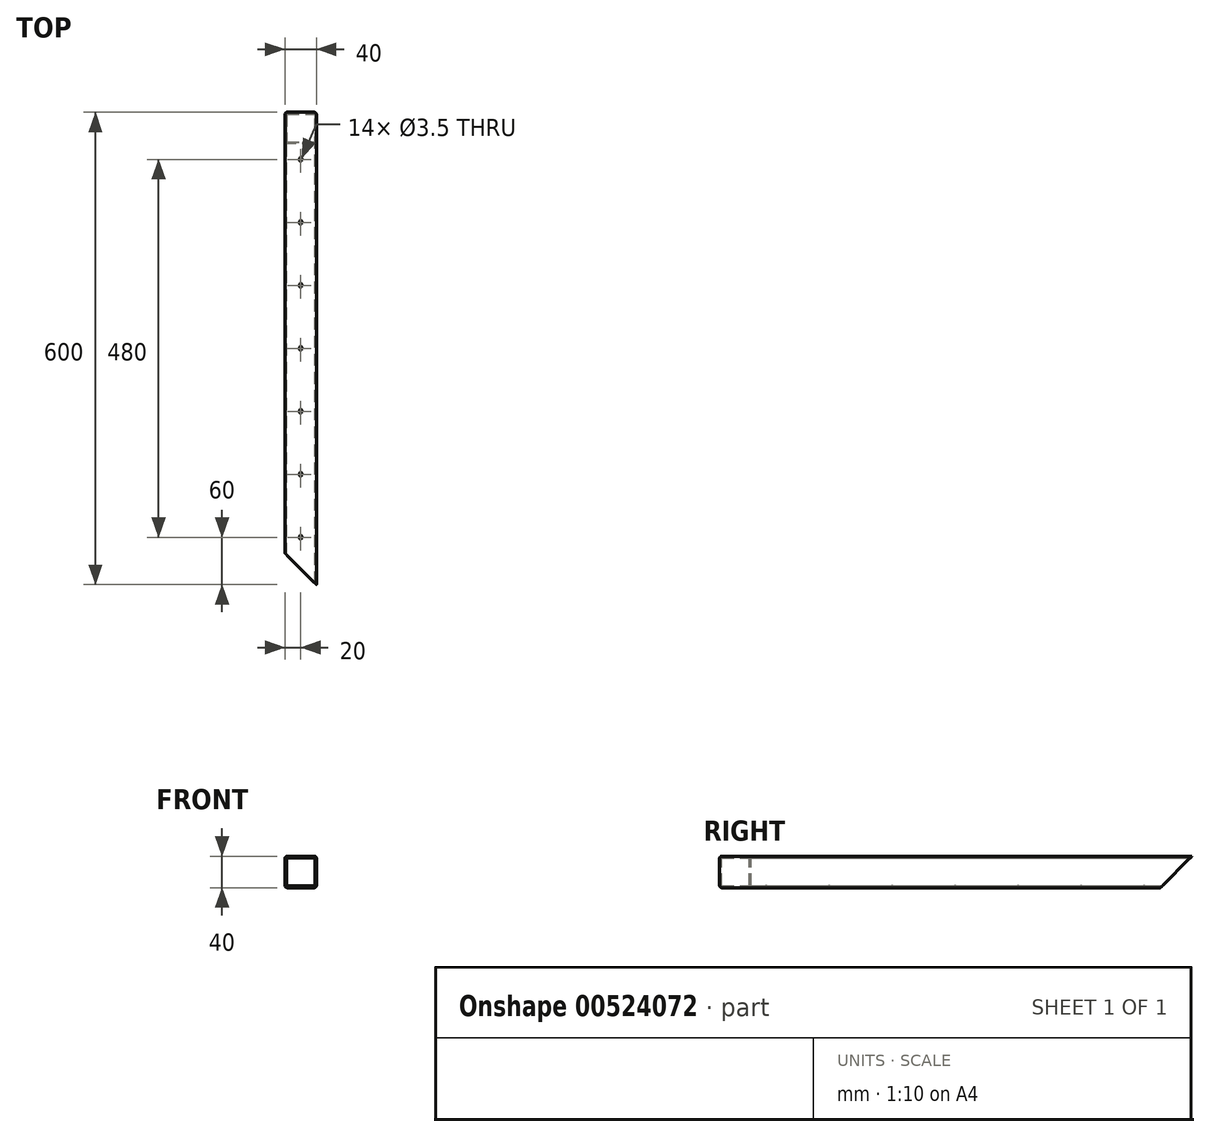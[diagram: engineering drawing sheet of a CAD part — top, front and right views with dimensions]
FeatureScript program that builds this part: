
annotation { "Feature Type Name" : "Feature", "Feature Type Description" : "" }
export const myFeature = defineFeature(function(context is Context, id is Id, definition is map)
    precondition{}
    {
        {
            assignVariable(context, id + "F0", {"name" : "R", "anyValue" : 3});
        }
        {
            assignVariable(context, id + "F1", {"name" : "W", "anyValue" : 2});
        }
        {
            var Q0;
            Q0=qCreatedBy(makeId("Front.planeOp"),FACE);
            var sketch = newSketch(context, id + "F2", { "sketchPlane" : qUnion([Q0])});
            skLineSegment(sketch, "E0.bottom", {"start": v(-20, 20) * mm, "end": v(20, 20) * mm});
            skLineSegment(sketch, "E0.top", {"start": v(-20, -20) * mm, "end": v(20, -20) * mm});
            skLineSegment(sketch, "E0.left", {"start": v(-20, 20) * mm, "end": v(-20, -20) * mm});
            skLineSegment(sketch, "E0.right", {"start": v(20, 20) * mm, "end": v(20, -20) * mm});
            skSolve(sketch);
        }
        {
            var Q0;
            Q0=qSketchRegion(id+"F2",true);
            extrude(context, id + "F3", {"entities" : qUnion([Q0]), "endBound" : BoundingType.SYMMETRIC, "depth" : 600 * mm, "offsetDistance" : 25 * mm});
        }
        {
            var Q0;
            Q0=makeQuery(id+"F3.opExtrude","SWEPT_EDGE",EDGE,{"disambiguationData":[OSD([sQuery(id+"F2.wireOp",EDGE,"E0.bottom"),sQuery(id+"F2.wireOp",EDGE,"E0.right")])]});
            var Q1;
            Q1=makeQuery(id+"F3.opExtrude","SWEPT_EDGE",EDGE,{"disambiguationData":[OSD([sQuery(id+"F2.wireOp",EDGE,"E0.bottom"),sQuery(id+"F2.wireOp",EDGE,"E0.left")])]});
            var Q2;
            Q2=makeQuery(id+"F3.opExtrude","SWEPT_EDGE",EDGE,{"disambiguationData":[OSD([sQuery(id+"F2.wireOp",EDGE,"E0.top"),sQuery(id+"F2.wireOp",EDGE,"E0.right")])]});
            var Q3;
            Q3=makeQuery(id+"F3.opExtrude","SWEPT_EDGE",EDGE,{"disambiguationData":[OSD([sQuery(id+"F2.wireOp",EDGE,"E0.top"),sQuery(id+"F2.wireOp",EDGE,"E0.left")])]});
            fillet(context, id + "F4", {"entities" : qUnion([Q0, Q1, Q2, Q3]), "radius" : (getVariable(context, 'R')) * mm, "tangentPropagation" : true, "allowEdgeOverflow" : false});
        }
        {
            var Q0;
            Q0=makeQuery(id+"F3.opExtrude","CAP_FACE",FACE,{"disambiguationData":[OSD([sQuery(id+"F2.wireOp",EDGE,"E0.bottom"),sQuery(id+"F2.wireOp",EDGE,"E0.top"),sQuery(id+"F2.wireOp",EDGE,"E0.left"),sQuery(id+"F2.wireOp",EDGE,"E0.right")])],"isStart":false});
            var Q1;
            Q1=makeQuery(id+"F3.opExtrude","CAP_FACE",FACE,{"disambiguationData":[OSD([sQuery(id+"F2.wireOp",EDGE,"E0.bottom"),sQuery(id+"F2.wireOp",EDGE,"E0.top"),sQuery(id+"F2.wireOp",EDGE,"E0.left"),sQuery(id+"F2.wireOp",EDGE,"E0.right")])],"isStart":true});
            shell(context, id + "F5", {"entities" : qUnion([Q0, Q1]), "thickness" : (getVariable(context, 'W')) * mm});
        }
        {
            var Q0;
            Q0=makeQuery(id+"F3.opExtrude","SWEPT_FACE",FACE,{"disambiguationData":[OSD([sQuery(id+"F2.wireOp",EDGE,"E0.left")])]});
            var sketch = newSketch(context, id + "F6", { "sketchPlane" : qUnion([Q0])});
            skLineSegment(sketch, "E1", {"start": v(-300, -20) * mm, "end": v(-260, -20) * mm});
            skLineSegment(sketch, "E2", {"start": v(-260, -20) * mm, "end": v(-300, 20) * mm});
            skLineSegment(sketch, "E3", {"start": v(-300, 20) * mm, "end": v(-300, -20) * mm});
            skSolve(sketch);
        }
        {
            var Q0;
            Q0=qSketchRegion(id+"F6",true);
            extrude(context, id + "F7", {"entities" : qUnion([Q0]), "operationType" : NewBodyOperationType.REMOVE, "endBound" : BoundingType.THROUGH_ALL, "oppositeDirection" : true, "depth" : 25 * mm, "offsetDistance" : 25 * mm});
        }
        {
            var Q0;
            Q0=makeQuery(id+"F3.opExtrude","SWEPT_FACE",FACE,{"disambiguationData":[OSD([sQuery(id+"F2.wireOp",EDGE,"E0.bottom")])]});
            var sketch = newSketch(context, id + "F8", { "sketchPlane" : qUnion([Q0])});
            skLineSegment(sketch, "E4.0", {"start": v(20, 297) * mm, "end": v(20, -300) * mm, "construction": true});
            skLineSegment(sketch, "E5", {"start": v(-20, -300) * mm, "end": v(20, -300) * mm});
            skLineSegment(sketch, "E6", {"start": v(20, -300) * mm, "end": v(-20, -260) * mm});
            skLineSegment(sketch, "E7", {"start": v(-20, -260) * mm, "end": v(-20, -300) * mm});
            skSolve(sketch);
        }
        {
            var Q0;
            Q0=qSketchRegion(id+"F8",true);
            extrude(context, id + "F9", {"entities" : qUnion([Q0]), "operationType" : NewBodyOperationType.REMOVE, "endBound" : BoundingType.THROUGH_ALL, "oppositeDirection" : true, "depth" : 25 * mm, "offsetDistance" : 25 * mm});
        }
        {
            var Q0;
            Q0=makeQuery(id+"F3.opExtrude","SWEPT_FACE",FACE,{"disambiguationData":[OSD([sQuery(id+"F2.wireOp",EDGE,"E0.top")])]});
            var sketch = newSketch(context, id + "F10", { "sketchPlane" : qUnion([Q0])});
            skPoint(sketch, "E8", {"position": v(0, 0) * mm});
            skPoint(sketch, "E9", {"position": v(0, -80) * mm});
            skPoint(sketch, "E10", {"position": v(0, -160) * mm});
            skPoint(sketch, "E11", {"position": v(0, -240) * mm});
            skPoint(sketch, "E12", {"position": v(0, 80) * mm});
            skPoint(sketch, "E13", {"position": v(0, 160) * mm});
            skPoint(sketch, "E14", {"position": v(0, 240) * mm});
            skSolve(sketch);
        }
        {
            var Q0;
            Q0=sQuery(id+"F10.wireOp",VERTEX,"E11");
            var Q1;
            Q1=sQuery(id+"F10.wireOp",VERTEX,"E10");
            var Q2;
            Q2=sQuery(id+"F10.wireOp",VERTEX,"E9");
            var Q3;
            Q3=sQuery(id+"F10.wireOp",VERTEX,"E8");
            var Q4;
            Q4=sQuery(id+"F10.wireOp",VERTEX,"E12");
            var Q5;
            Q5=sQuery(id+"F10.wireOp",VERTEX,"E13");
            var Q6;
            Q6=sQuery(id+"F10.wireOp",VERTEX,"E14");
            var Q7;
            Q7=makeQuery(id+"F3.opExtrude","SWEPT_BODY",BODY,{"disambiguationData":[OSD([sQuery(id+"F2.wireOp",EDGE,"E0.bottom"),sQuery(id+"F2.wireOp",EDGE,"E0.top"),sQuery(id+"F2.wireOp",EDGE,"E0.left"),sQuery(id+"F2.wireOp",EDGE,"E0.right")])]});
            hole(context, id + "F11", {"style" : HoleStyle.C_SINK, "endStyle" : HoleEndStyle.THROUGH, "holeDiameter" : 3.5 * mm, "cSinkDiameter" : 6 * mm, "cSinkAngle" : 90 * degree, "isTappedThrough" : true, "tappedDepth" : 12 * mm, "tapClearance" : 3, "locations" : qUnion([Q0, Q1, Q2, Q3, Q4, Q5, Q6]), "scope" : qUnion([Q7])});
        }
    });
